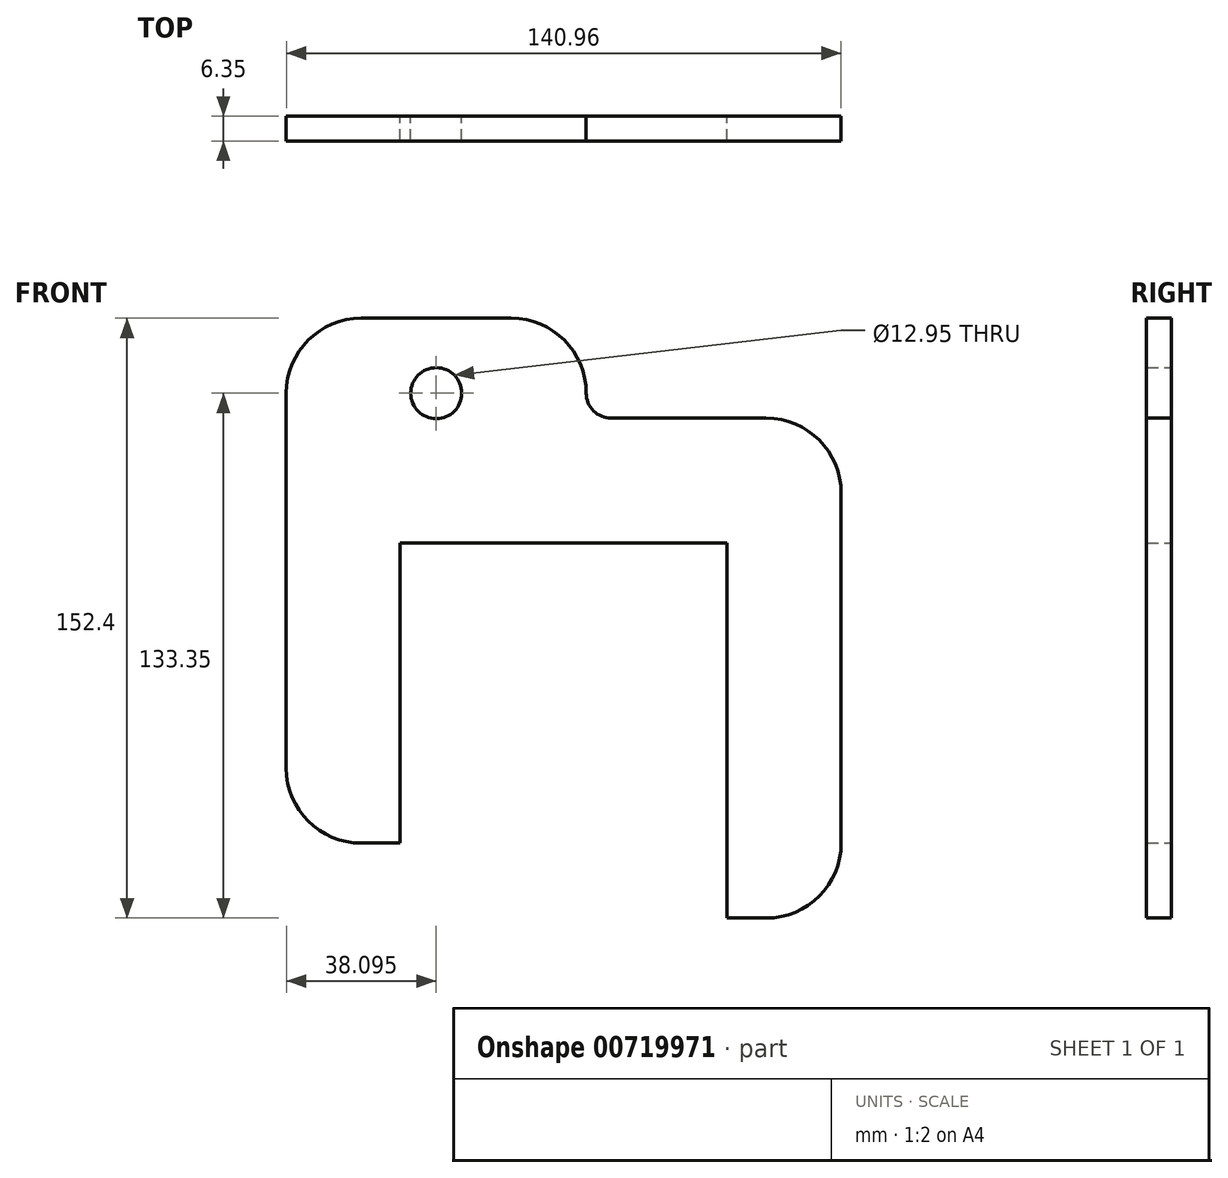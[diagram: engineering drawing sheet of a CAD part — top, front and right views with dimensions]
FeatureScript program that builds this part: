
annotation { "Feature Type Name" : "Feature", "Feature Type Description" : "" }
export const myFeature = defineFeature(function(context is Context, id is Id, definition is map)
    precondition{}
    {
        {
            var Q0;
            Q0=qCreatedBy(makeId("Front.planeOp"),FACE);
            var sketch = newSketch(context, id + "F0", { "sketchPlane" : qUnion([Q0])});
            skLineSegment(sketch, "E0.bottom", {"start": v(51.44, -76.2) * mm, "end": v(41.53, -76.2) * mm});
            skLineSegment(sketch, "E0.top", {"start": v(-13.34, 76.2) * mm, "end": v(-51.44, 76.2) * mm});
            skLineSegment(sketch, "E0.left", {"start": v(70.49, -57.15) * mm, "end": v(70.48, 31.75) * mm});
            skLineSegment(sketch, "E0.right", {"start": v(-70.48, -38.1) * mm, "end": v(-70.49, 57.15) * mm});
            skPoint(sketch, "E0.middle", {"position": v(0, 0) * mm});
            skLineSegment(sketch, "E1", {"start": v(-41.53, 19.05) * mm, "end": v(-41.53, -57.15) * mm});
            skLineSegment(sketch, "E2", {"start": v(-41.53, 19.05) * mm, "end": v(41.53, 19.05) * mm});
            skLineSegment(sketch, "E3", {"start": v(41.53, 19.05) * mm, "end": v(41.53, -76.2) * mm});
            skCircle(sketch, "E4", {"center": v(-32.39, 57.15) * mm, "radius": 6.48 * mm});
            skPoint(sketch, "E5.visualSharp", {"position": v(-70.48, -76.2) * mm});
            skPoint(sketch, "E6.visualSharp", {"position": v(70.49, -76.2) * mm});
            skArc(sketch, "E6.filletArc", {"start": v(51.44, -76.2) * mm, "mid": v(64.9, -70.62) * mm, "end": v(70.49, -57.15) * mm});
            skPoint(sketch, "E7.visualSharp", {"position": v(70.48, 76.2) * mm});
            skArc(sketch, "E7.filletArc", {"start": v(70.48, 57.15) * mm, "mid": v(64.9, 70.62) * mm, "end": v(51.44, 76.2) * mm});
            skPoint(sketch, "E8.visualSharp", {"position": v(-70.49, 76.2) * mm});
            skArc(sketch, "E8.filletArc", {"start": v(-51.44, 76.2) * mm, "mid": v(-64.9, 70.62) * mm, "end": v(-70.49, 57.15) * mm});
            skLineSegment(sketch, "E9", {"start": v(51.43, 50.8) * mm, "end": v(12.06, 50.8) * mm});
            skLineSegment(sketch, "E10", {"start": v(5.71, 57.15) * mm, "end": v(5.71, 57.15) * mm});
            skArc(sketch, "E11.filletArc", {"start": v(70.48, 31.75) * mm, "mid": v(64.9, 45.22) * mm, "end": v(51.43, 50.8) * mm});
            skPoint(sketch, "E12.visualSharp", {"position": v(5.71, 50.8) * mm});
            skArc(sketch, "E12.filletArc", {"start": v(5.71, 57.15) * mm, "mid": v(7.57, 52.66) * mm, "end": v(12.06, 50.8) * mm});
            skArc(sketch, "E13.filletArc", {"start": v(5.71, 57.15) * mm, "mid": v(0.14, 70.62) * mm, "end": v(-13.34, 76.2) * mm});
            skPoint(sketch, "E14", {"position": v(-41.53, -57.15) * mm});
            skLineSegment(sketch, "E15", {"start": v(-41.53, -57.15) * mm, "end": v(-51.43, -57.15) * mm});
            skPoint(sketch, "E16.orphan", {"position": v(-41.53, -76.2) * mm});
            skPoint(sketch, "E17.visualSharp", {"position": v(-70.48, -57.15) * mm});
            skArc(sketch, "E17.filletArc", {"start": v(-70.48, -38.1) * mm, "mid": v(-64.9, -51.57) * mm, "end": v(-51.43, -57.15) * mm});
            skSolve(sketch);
        }
        {
            var Q0;
            Q0=makeQuery(id+"F0.imprint","IMPRINT",FACE,{"disambiguationData":[TD([[makeQuery(id+"F0.imprint","IMPRINT",EDGE,{"derivedFrom":sQuery(id+"F0.wireOp",EDGE,"E0.bottom")}),-1.0]])]});
            extrude(context, id + "F1", {"entities" : qUnion([Q0]), "depth" : 6.35 * mm, "offsetDistance" : 25.4 * mm});
        }
    });
